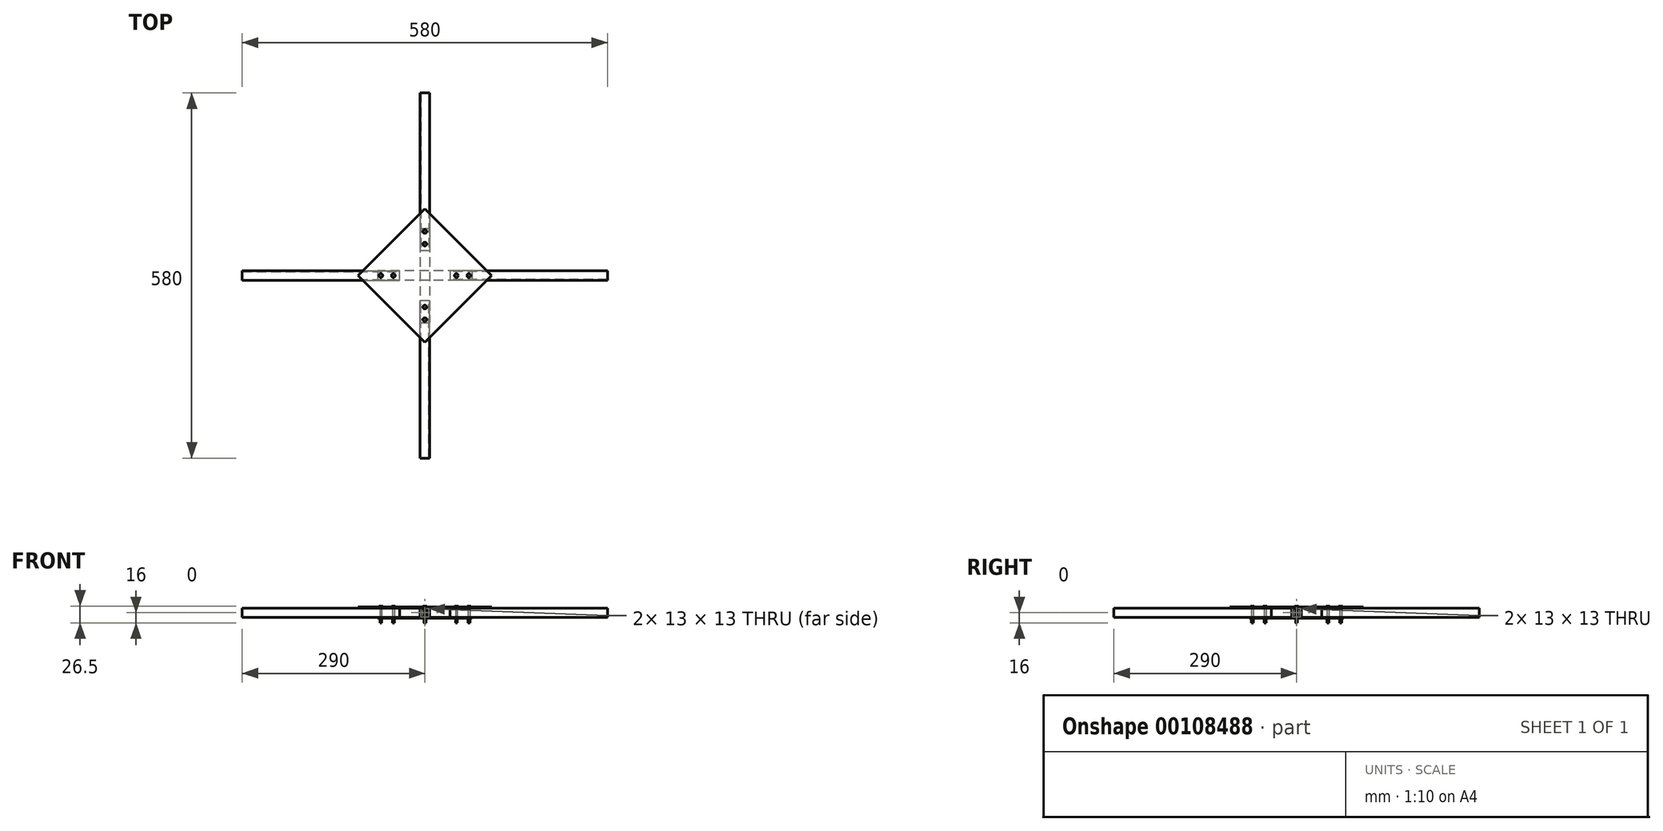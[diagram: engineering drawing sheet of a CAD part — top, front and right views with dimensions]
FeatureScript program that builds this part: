
annotation { "Feature Type Name" : "Feature", "Feature Type Description" : "" }
export const myFeature = defineFeature(function(context is Context, id is Id, definition is map)
    precondition{}
    {
        {
            var Q0;
            Q0=qCreatedBy(makeId("Right.planeOp"),FACE);
            var sketch = newSketch(context, id + "F0", { "sketchPlane" : qUnion([Q0])});
            skLineSegment(sketch, "E0.rect.bottom", {"start": v(6.5, -6.5) * mm, "end": v(-6.5, -6.5) * mm});
            skLineSegment(sketch, "E0.rect.top", {"start": v(6.5, 6.5) * mm, "end": v(-6.5, 6.5) * mm});
            skLineSegment(sketch, "E0.rect.left", {"start": v(6.5, -6.5) * mm, "end": v(6.5, 6.5) * mm});
            skLineSegment(sketch, "E0.rect.right", {"start": v(-6.5, -6.5) * mm, "end": v(-6.5, 6.5) * mm});
            skPoint(sketch, "E0.rect.middle", {"position": v(0, 0) * mm});
            skLineSegment(sketch, "E1.rect.bottom", {"start": v(7.5, 7.5) * mm, "end": v(-7.5, 7.5) * mm});
            skLineSegment(sketch, "E1.rect.top", {"start": v(7.5, -7.5) * mm, "end": v(-7.5, -7.5) * mm});
            skLineSegment(sketch, "E1.rect.left", {"start": v(7.5, 7.5) * mm, "end": v(7.5, -7.5) * mm});
            skLineSegment(sketch, "E1.rect.right", {"start": v(-7.5, 7.5) * mm, "end": v(-7.5, -7.5) * mm});
            skLineSegment(sketch, "E2", {"start": v(0, 0) * mm, "end": v(-51.77, 0) * mm, "construction": true});
            skLineSegment(sketch, "E3", {"start": v(0, 0) * mm, "end": v(0, 56.47) * mm, "construction": true});
            skSolve(sketch);
        }
        {
            var Q0;
            Q0=qSketchRegion(id+"F0",true);
            extrude(context, id + "F1", {"entities" : qUnion([Q0]), "depth" : 250 * mm});
        }
        {
            var Q0;
            Q0=makeQuery(id+"F1.opExtrude","SWEPT_BODY",BODY,{"disambiguationData":[OSD([sQuery(id+"F0.wireOp",EDGE,"E0.rect.bottom"),sQuery(id+"F0.wireOp",EDGE,"E0.rect.top"),sQuery(id+"F0.wireOp",EDGE,"E0.rect.left"),sQuery(id+"F0.wireOp",EDGE,"E0.rect.right"),sQuery(id+"F0.wireOp",EDGE,"E1.rect.bottom"),sQuery(id+"F0.wireOp",EDGE,"E1.rect.top"),sQuery(id+"F0.wireOp",EDGE,"E1.rect.left"),sQuery(id+"F0.wireOp",EDGE,"E1.rect.right")])]});
            transform(context, id + "F2", {"entities" : qUnion([Q0]), "transformType" : TransformType.TRANSLATION_3D, "dx" : 40 * mm, "dy" : 0 * mm, "dz" : 0 * mm, "makeCopy" : false});
        }
        {
            var Q0;
            Q0=makeQuery(id+"F1.opExtrude","SWEPT_BODY",BODY,{"disambiguationData":[OSD([sQuery(id+"F0.wireOp",EDGE,"E0.rect.bottom"),sQuery(id+"F0.wireOp",EDGE,"E0.rect.top"),sQuery(id+"F0.wireOp",EDGE,"E0.rect.left"),sQuery(id+"F0.wireOp",EDGE,"E0.rect.right"),sQuery(id+"F0.wireOp",EDGE,"E1.rect.bottom"),sQuery(id+"F0.wireOp",EDGE,"E1.rect.top"),sQuery(id+"F0.wireOp",EDGE,"E1.rect.left"),sQuery(id+"F0.wireOp",EDGE,"E1.rect.right")])]});
            var Q1;
            Q1=sQuery(id+"F0.wireOp",EDGE,"E3");
            circularPattern(context, id + "F3", {"entities" : qUnion([Q0]), "axis" : qUnion([Q1]), "angle" : 90 * degree, "instanceCount" : 4});
        }
        {
            var Q0;
            Q0=makeQuery(id+"F3.opPattern","COPY",FACE,{"derivedFrom":makeQuery(id+"F1.opExtrude","SWEPT_FACE",FACE,{"disambiguationData":[OSD([sQuery(id+"F0.wireOp",EDGE,"E1.rect.bottom")])]}),"instanceName":"2"});
            var sketch = newSketch(context, id + "F4", { "sketchPlane" : qUnion([Q0])});
            skLineSegment(sketch, "E4.rect.bottom", {"start": v(75, -75) * mm, "end": v(-75, -75) * mm});
            skLineSegment(sketch, "E4.rect.top", {"start": v(75, 75) * mm, "end": v(-75, 75) * mm});
            skLineSegment(sketch, "E4.rect.left", {"start": v(75, -75) * mm, "end": v(75, 75) * mm});
            skLineSegment(sketch, "E4.rect.right", {"start": v(-75, -75) * mm, "end": v(-75, 75) * mm});
            skPoint(sketch, "E4.rect.middle", {"position": v(0, 0) * mm});
            skSolve(sketch);
        }
        {
            var Q0;
            Q0=qSketchRegion(id+"F4",true);
            extrude(context, id + "F5", {"entities" : qUnion([Q0]), "depth" : 1.5 * mm});
        }
        {
            var Q0;
            Q0=makeQuery(id+"F3.opPattern","COPY",FACE,{"derivedFrom":makeQuery(id+"F1.opExtrude","SWEPT_FACE",FACE,{"disambiguationData":[OSD([sQuery(id+"F0.wireOp",EDGE,"E1.rect.top")])]}),"instanceName":"1"});
            var sketch = newSketch(context, id + "F6", { "sketchPlane" : qUnion([Q0])});
            skLineSegment(sketch, "E5.rect.bottom", {"start": v(75, -7.5) * mm, "end": v(-75, -7.5) * mm});
            skLineSegment(sketch, "E5.rect.top", {"start": v(75, 7.5) * mm, "end": v(-75, 7.5) * mm});
            skLineSegment(sketch, "E5.rect.left", {"start": v(75, -7.5) * mm, "end": v(75, 7.5) * mm});
            skLineSegment(sketch, "E5.rect.right", {"start": v(-75, -7.5) * mm, "end": v(-75, 7.5) * mm});
            skPoint(sketch, "E5.rect.middle", {"position": v(0, 0) * mm});
            skSolve(sketch);
        }
        {
            var Q0;
            Q0=qSketchRegion(id+"F6",true);
            extrude(context, id + "F7", {"entities" : qUnion([Q0]), "depth" : 1.5 * mm});
        }
        {
            var Q0;
            Q0=makeQuery(id+"F5.opExtrude","SWEPT_BODY",BODY,{"disambiguationData":[OSD([sQuery(id+"F4.wireOp",EDGE,"E4.rect.bottom"),sQuery(id+"F4.wireOp",EDGE,"E4.rect.top"),sQuery(id+"F4.wireOp",EDGE,"E4.rect.left"),sQuery(id+"F4.wireOp",EDGE,"E4.rect.right")])]});
            var Q1;
            Q1=sQuery(id+"F0.wireOp",EDGE,"E3");
            transform(context, id + "F8", {"entities" : qUnion([Q0]), "transformType" : TransformType.ROTATION, "transformAxis" : qUnion([Q1]), "angle" : 45 * degree, "makeCopy" : false});
        }
        {
            var Q0;
            Q0=makeQuery(id+"F7.opExtrude","SWEPT_BODY",BODY,{"disambiguationData":[OSD([sQuery(id+"F6.wireOp",EDGE,"E5.rect.bottom"),sQuery(id+"F6.wireOp",EDGE,"E5.rect.top"),sQuery(id+"F6.wireOp",EDGE,"E5.rect.left"),sQuery(id+"F6.wireOp",EDGE,"E5.rect.right")])]});
            var Q1;
            Q1=sQuery(id+"F0.wireOp",EDGE,"E3");
            circularPattern(context, id + "F9", {"entities" : qUnion([Q0]), "axis" : qUnion([Q1]), "angle" : 90 * degree, "instanceCount" : 2});
        }
        {
            var Q0;
            Q0=qCreatedBy(makeId("Front.planeOp"),FACE);
            var sketch = newSketch(context, id + "F10", { "sketchPlane" : qUnion([Q0])});
            skLineSegment(sketch, "E6", {"start": v(0, 10.5) * mm, "end": v(3, 10.5) * mm});
            skLineSegment(sketch, "E7", {"start": v(3, 10.5) * mm, "end": v(3, 9) * mm});
            skLineSegment(sketch, "E8", {"start": v(3, 9) * mm, "end": v(1.5, 9) * mm});
            skLineSegment(sketch, "E9", {"start": v(1.5, 9) * mm, "end": v(1.5, -16) * mm});
            skLineSegment(sketch, "E10", {"start": v(1.5, -16) * mm, "end": v(0, -16) * mm});
            skLineSegment(sketch, "E11", {"start": v(0, 10.5) * mm, "end": v(0, -16) * mm});
            skSolve(sketch);
        }
        {
            var Q0;
            Q0=qSketchRegion(id+"F10",true);
            var Q1;
            Q1=sQuery(id+"F0.wireOp",EDGE,"E3");
            revolve(context, id + "F11", {"entities" : qUnion([Q0]), "axis" : qUnion([Q1]), "revolveType" : RevolveType.FULL});
        }
        {
            var Q0;
            Q0=makeQuery(id+"F11.opRevolve","SWEPT_BODY",BODY,{"disambiguationData":[OSD([sQuery(id+"F10.wireOp",EDGE,"E6"),sQuery(id+"F10.wireOp",EDGE,"E7"),sQuery(id+"F10.wireOp",EDGE,"E8"),sQuery(id+"F10.wireOp",EDGE,"E9"),sQuery(id+"F10.wireOp",EDGE,"E10"),sQuery(id+"F10.wireOp",EDGE,"E11")])]});
            transform(context, id + "F12", {"entities" : qUnion([Q0]), "transformType" : TransformType.TRANSLATION_3D, "dx" : 50 * mm, "dy" : 0 * mm, "dz" : 0 * mm, "makeCopy" : false});
        }
        {
            var Q0;
            Q0=makeQuery(id+"F11.opRevolve","SWEPT_BODY",BODY,{"disambiguationData":[OSD([sQuery(id+"F10.wireOp",EDGE,"E6"),sQuery(id+"F10.wireOp",EDGE,"E7"),sQuery(id+"F10.wireOp",EDGE,"E8"),sQuery(id+"F10.wireOp",EDGE,"E9"),sQuery(id+"F10.wireOp",EDGE,"E10"),sQuery(id+"F10.wireOp",EDGE,"E11")])]});
            transform(context, id + "F13", {"entities" : qUnion([Q0]), "transformType" : TransformType.TRANSLATION_3D, "dx" : 20 * mm, "dy" : 0 * mm, "dz" : 0 * mm, "makeCopy" : true});
        }
        {
            var Q0;
            Q0=makeQuery(id+"F11.opRevolve","SWEPT_BODY",BODY,{"disambiguationData":[OSD([sQuery(id+"F10.wireOp",EDGE,"E6"),sQuery(id+"F10.wireOp",EDGE,"E7"),sQuery(id+"F10.wireOp",EDGE,"E8"),sQuery(id+"F10.wireOp",EDGE,"E9"),sQuery(id+"F10.wireOp",EDGE,"E10"),sQuery(id+"F10.wireOp",EDGE,"E11")])]});
            var Q1;
            Q1=makeQuery(id+"F13.opPattern","COPY",BODY,{"derivedFrom":makeQuery(id+"F11.opRevolve","SWEPT_BODY",BODY,{"disambiguationData":[OSD([sQuery(id+"F10.wireOp",EDGE,"E6"),sQuery(id+"F10.wireOp",EDGE,"E7"),sQuery(id+"F10.wireOp",EDGE,"E8"),sQuery(id+"F10.wireOp",EDGE,"E9"),sQuery(id+"F10.wireOp",EDGE,"E10"),sQuery(id+"F10.wireOp",EDGE,"E11")])]}),"instanceName":"1"});
            var Q2;
            Q2=sQuery(id+"F0.wireOp",EDGE,"E3");
            circularPattern(context, id + "F14", {"entities" : qUnion([Q0, Q1]), "axis" : qUnion([Q2]), "angle" : 90 * degree, "instanceCount" : 4});
        }
    });
